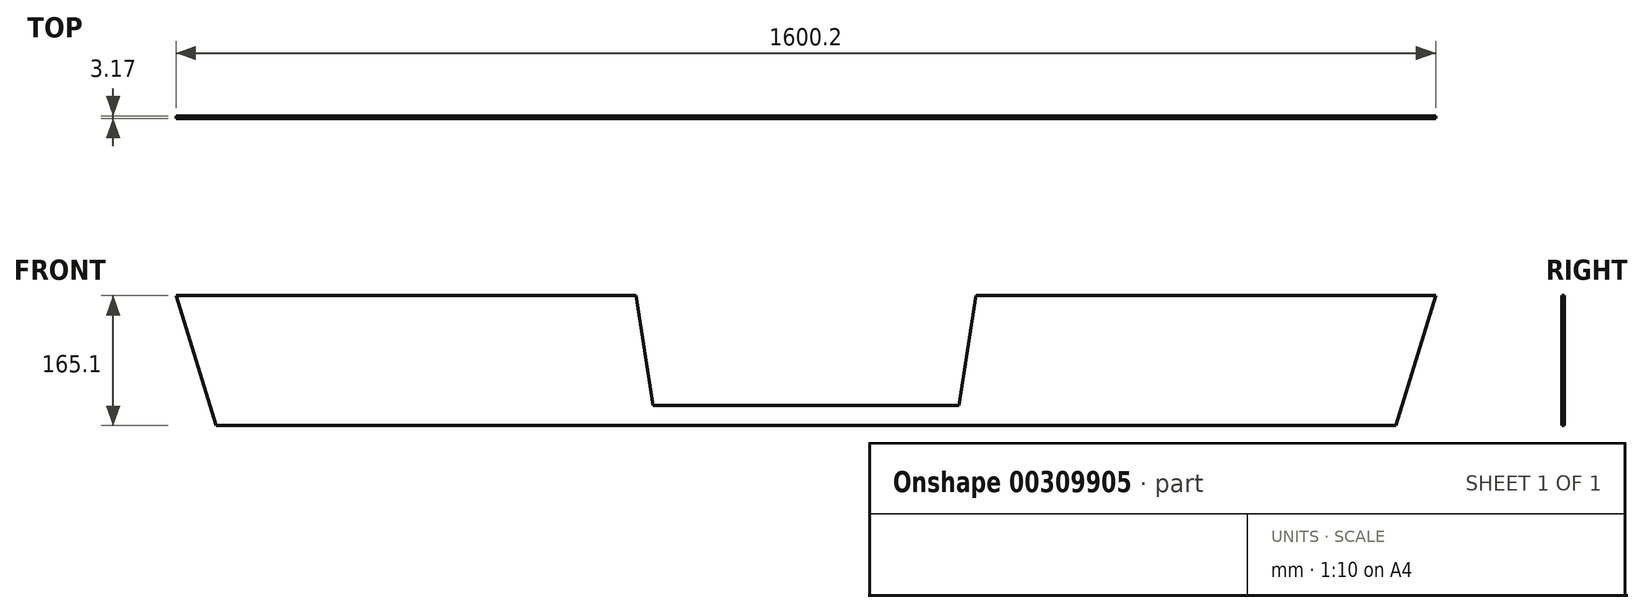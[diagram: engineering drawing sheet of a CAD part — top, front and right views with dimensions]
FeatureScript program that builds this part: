
annotation { "Feature Type Name" : "Feature", "Feature Type Description" : "" }
export const myFeature = defineFeature(function(context is Context, id is Id, definition is map)
    precondition{}
    {
        {
            var Q0;
            Q0=qCreatedBy(makeId("Front.planeOp"),FACE);
            cPlane(context, id + "F0", {"entities" : qUnion([Q0]), "cplaneType" : CPlaneType.OFFSET, "offset" : 25.4 * mm, "width" : 152.4 * mm, "height" : 152.4 * mm});
        }
        {
            var Q0;
            Q0=qCreatedBy(id+"F0.planeOp",FACE);
            var sketch = newSketch(context, id + "F1", { "sketchPlane" : qUnion([Q0])});
            skLineSegment(sketch, "E0.bottom", {"start": v(0, 0) * mm, "end": v(584.2, 0) * mm});
            skLineSegment(sketch, "E0.top", {"start": v(50.8, -165.1) * mm, "end": v(1549.4, -165.1) * mm});
            skLineSegment(sketch, "E1", {"start": v(50.8, -165.1) * mm, "end": v(0, 0) * mm});
            skLineSegment(sketch, "E2", {"start": v(1549.4, -165.1) * mm, "end": v(1600.2, 0) * mm});
            skLineSegment(sketch, "E3", {"start": v(605.7, -139.7) * mm, "end": v(584.2, 0) * mm});
            skLineSegment(sketch, "E4", {"start": v(994.5, -139.7) * mm, "end": v(1016, 0) * mm});
            skLineSegment(sketch, "E5", {"start": v(800.1, -139.7) * mm, "end": v(994.5, -139.7) * mm});
            skLineSegment(sketch, "E6", {"start": v(800.1, -139.7) * mm, "end": v(605.7, -139.7) * mm});
            skLineSegment(sketch, "E7.trimOffspring", {"start": v(1016, 0) * mm, "end": v(1600.2, 0) * mm});
            skSolve(sketch);
        }
        {
            var Q0;
            Q0=makeQuery(id+"F1.imprint","IMPRINT",FACE,{"disambiguationData":[TD([[makeQuery(id+"F1.imprint","IMPRINT",EDGE,{"derivedFrom":sQuery(id+"F1.wireOp",EDGE,"E0.top")}),1.0]])]});
            extrude(context, id + "F2", {"entities" : qUnion([Q0]), "depth" : 3.17 * mm});
        }
    });
